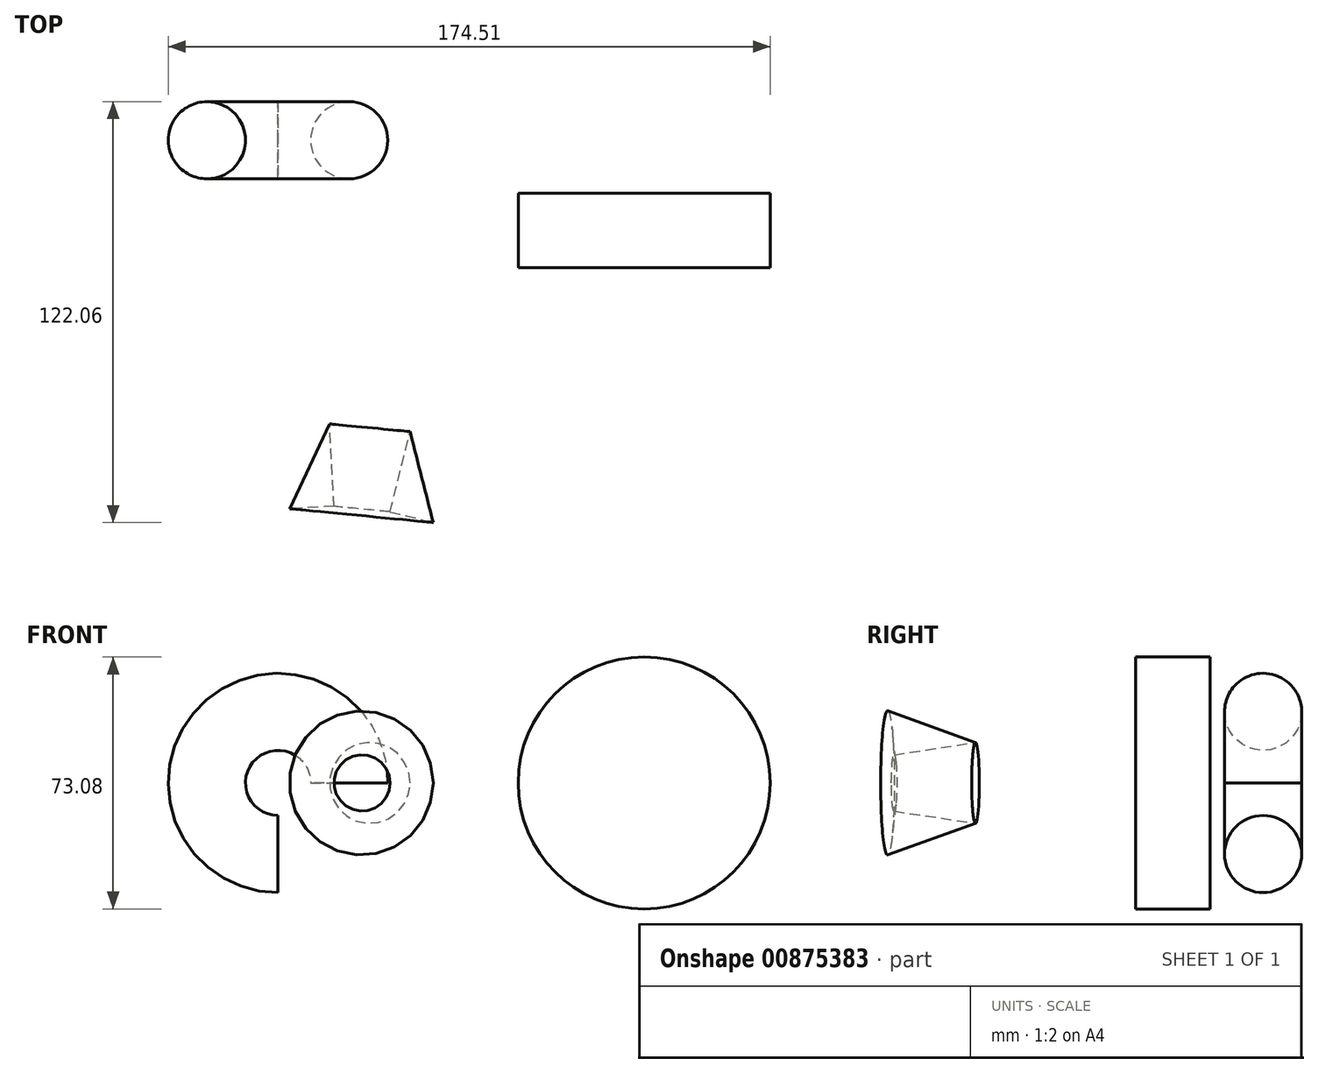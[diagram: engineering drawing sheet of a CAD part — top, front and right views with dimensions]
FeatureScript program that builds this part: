
annotation { "Feature Type Name" : "Feature", "Feature Type Description" : "" }
export const myFeature = defineFeature(function(context is Context, id is Id, definition is map)
    precondition{}
    {
        {
            var Q0;
            Q0=qCreatedBy(makeId("Top.planeOp"),FACE);
            var sketch = newSketch(context, id + "F0", { "sketchPlane" : qUnion([Q0])});
            skCircle(sketch, "E0", {"center": v(-62.28, 52.52) * mm, "radius": 11.18 * mm});
            skLineSegment(sketch, "E1.bottom", {"start": v(23.25, 37.16) * mm, "end": v(59.79, 37.16) * mm});
            skLineSegment(sketch, "E1.top", {"start": v(23.25, 15.57) * mm, "end": v(59.79, 15.57) * mm});
            skLineSegment(sketch, "E1.left", {"start": v(23.25, 37.16) * mm, "end": v(23.25, 15.57) * mm});
            skLineSegment(sketch, "E1.right", {"start": v(59.79, 37.16) * mm, "end": v(59.79, 15.57) * mm});
            skLineSegment(sketch, "E2", {"start": v(-55, -17.45) * mm, "end": v(-20.95, -29.08) * mm});
            skLineSegment(sketch, "E3", {"start": v(-20.95, -29.08) * mm, "end": v(-20.95, -63.13) * mm});
            skLineSegment(sketch, "E4", {"start": v(-20.95, -63.13) * mm, "end": v(-59.98, -69.35) * mm});
            skLineSegment(sketch, "E5", {"start": v(-59.98, -69.35) * mm, "end": v(-55, -17.45) * mm});
            skLineSegment(sketch, "E6", {"start": v(-44.62, -31.99) * mm, "end": v(-50.43, -55.24) * mm});
            skLineSegment(sketch, "E7", {"start": v(-50.43, -55.24) * mm, "end": v(-37.93, -58.36) * mm});
            skLineSegment(sketch, "E8", {"start": v(-37.93, -58.36) * mm, "end": v(-44.62, -31.99) * mm});
            skLineSegment(sketch, "E9", {"start": v(-82.91, 71.7) * mm, "end": v(-82.91, 30.26) * mm, "construction": true});
            skSolve(sketch);
        }
        {
            var Q0;
            Q0=makeQuery(id+"F0.imprint","IMPRINT",FACE,{"disambiguationData":[TD([[makeQuery(id+"F0.imprint","IMPRINT",EDGE,{"derivedFrom":sQuery(id+"F0.wireOp",EDGE,"E1.bottom")}),-1.0]])]});
            var Q1;
            Q1=sQuery(id+"F0.wireOp",EDGE,"E1.left");
            revolve(context, id + "F1", {"surfaceOperationType" : NewSurfaceOperationType.NEW, "entities" : qUnion([Q0]), "axis" : qUnion([Q1]), "revolveType" : RevolveType.FULL});
        }
        {
            var Q0;
            Q0=makeQuery(id+"F0.imprint","IMPRINT",FACE,{"disambiguationData":[TD([[makeQuery(id+"F0.imprint","IMPRINT",EDGE,{"derivedFrom":sQuery(id+"F0.wireOp",EDGE,"E0")}),1.0]])]});
            var Q1;
            Q1=sQuery(id+"F0.wireOp",EDGE,"E9");
            revolve(context, id + "F2", {"surfaceOperationType" : NewSurfaceOperationType.NEW, "entities" : qUnion([Q0]), "axis" : qUnion([Q1]), "revolveType" : RevolveType.ONE_DIRECTION, "angle" : 270 * degree});
        }
        {
            var Q0;
            Q0=makeQuery(id+"F0.imprint","IMPRINT",FACE,{"disambiguationData":[TD([[makeQuery(id+"F0.imprint","IMPRINT",EDGE,{"derivedFrom":sQuery(id+"F0.wireOp",EDGE,"E6")}),1.0]])]});
            var Q1;
            Q1=sQuery(id+"F0.wireOp",EDGE,"E5");
            revolve(context, id + "F3", {"surfaceOperationType" : NewSurfaceOperationType.NEW, "entities" : qUnion([Q0]), "axis" : qUnion([Q1]), "revolveType" : RevolveType.FULL});
        }
    });
